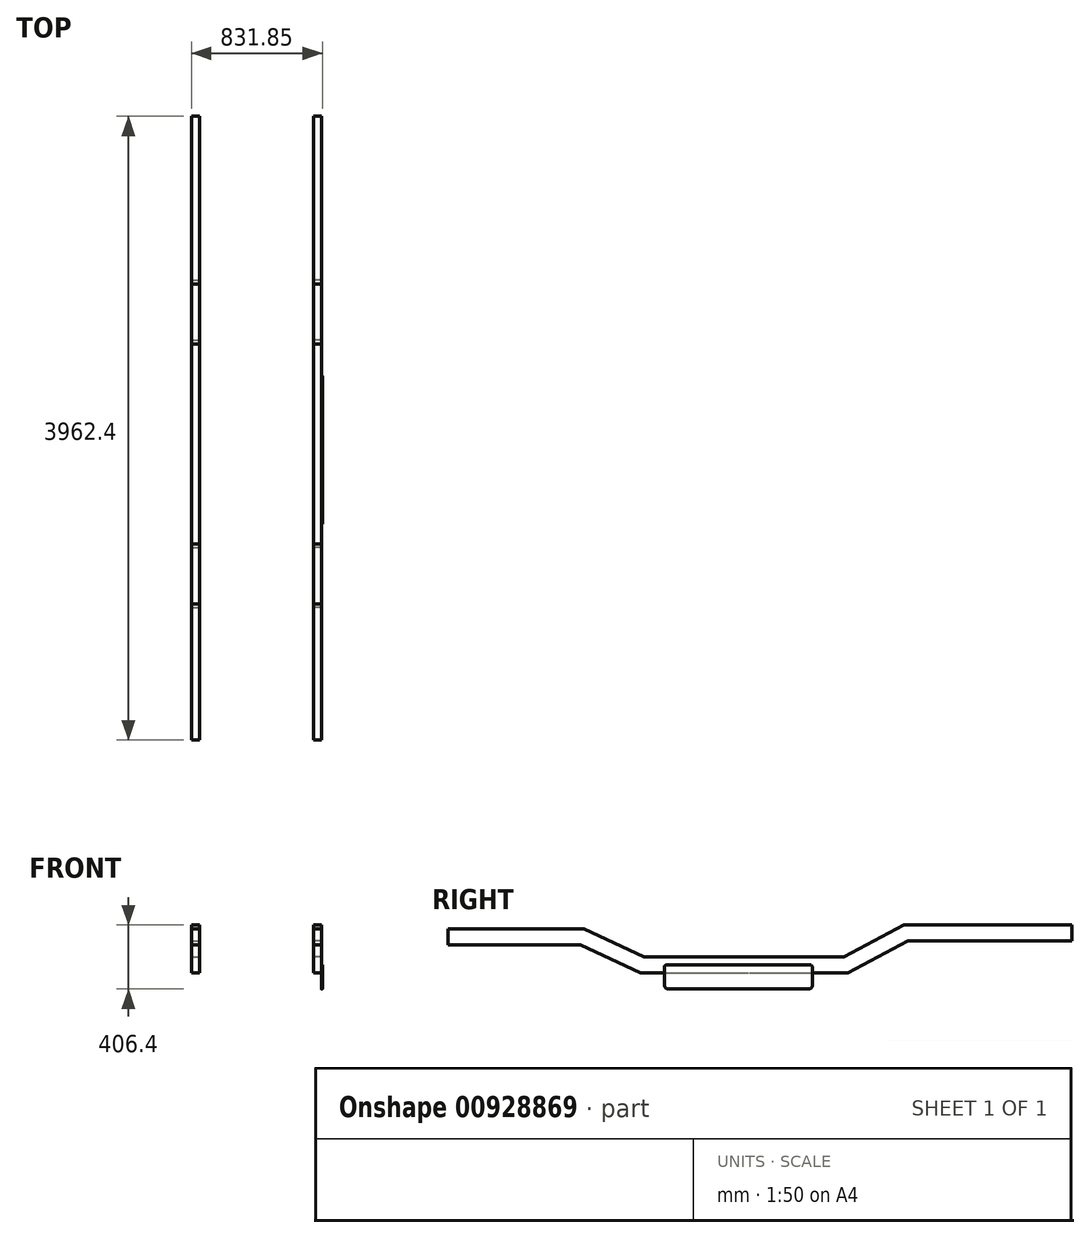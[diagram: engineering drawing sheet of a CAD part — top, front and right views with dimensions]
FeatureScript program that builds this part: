
annotation { "Feature Type Name" : "Feature", "Feature Type Description" : "" }
export const myFeature = defineFeature(function(context is Context, id is Id, definition is map)
    precondition{}
    {
        {
            var Q0;
            Q0=qCreatedBy(makeId("Right.planeOp"),FACE);
            var sketch = newSketch(context, id + "F0", { "sketchPlane" : qUnion([Q0])});
            skLineSegment(sketch, "E0", {"start": v(-1881.03, 279.4) * mm, "end": v(-1017.43, 279.4) * mm});
            skLineSegment(sketch, "E1", {"start": v(-1881.03, 177.8) * mm, "end": v(-1039.97, 177.8) * mm});
            skLineSegment(sketch, "E2", {"start": v(-1881.03, 177.8) * mm, "end": v(-1881.03, 279.4) * mm});
            skLineSegment(sketch, "E3", {"start": v(-1039.97, 177.8) * mm, "end": v(-658.97, 0) * mm});
            skLineSegment(sketch, "E4", {"start": v(-658.97, 0) * mm, "end": v(658.97, 0) * mm});
            skLineSegment(sketch, "E5", {"start": v(658.97, 0) * mm, "end": v(1039.97, 203.2) * mm});
            skLineSegment(sketch, "E6", {"start": v(1039.97, 203.2) * mm, "end": v(2081.37, 203.2) * mm});
            skLineSegment(sketch, "E7", {"start": v(2081.37, 203.2) * mm, "end": v(2081.37, 304.8) * mm});
            skLineSegment(sketch, "E8", {"start": v(2081.37, 304.8) * mm, "end": v(1014.57, 304.8) * mm});
            skLineSegment(sketch, "E9", {"start": v(1014.57, 304.8) * mm, "end": v(633.57, 101.6) * mm});
            skLineSegment(sketch, "E10", {"start": v(633.57, 101.6) * mm, "end": v(-636.43, 101.6) * mm});
            skLineSegment(sketch, "E11", {"start": v(-636.43, 101.6) * mm, "end": v(-1017.43, 279.4) * mm});
            skLineSegment(sketch, "E12", {"start": v(-849.47, 88.9) * mm, "end": v(-806.5, 180.97) * mm, "construction": true});
            skLineSegment(sketch, "E13", {"start": v(849.47, 101.6) * mm, "end": v(801.66, 191.25) * mm, "construction": true});
            skSolve(sketch);
        }
        {
            var Q0;
            Q0 = qSketchRegion(id + "F0", true);
            var Q1;
            Q1 = qSketchRegion(id + "F2", true);
            extrude(context, id + "F1", {"entities" : qUnion([Q0, Q1]), "oppositeDirection" : true, "depth" : 412.75 * mm, "offsetDistance" : 25.4 * mm});
        }
        {
            var Q0;
            Q0=makeQuery(id+"F1.opExtrude","SWEPT_FACE",FACE,{"disambiguationData":[OSD([sQuery(id+"F0.wireOp",EDGE,"E10")])]});
            var sketch = newSketch(context, id + "F2", { "sketchPlane" : qUnion([Q0])});
            skLineSegment(sketch, "E14", {"start": v(0, -2159) * mm, "end": v(0, 2159) * mm});
            skLineSegment(sketch, "E15", {"start": v(0, 2159) * mm, "end": v(-361.95, 2159) * mm});
            skLineSegment(sketch, "E16", {"start": v(-361.95, 2159) * mm, "end": v(-361.95, -2159) * mm});
            skLineSegment(sketch, "E17", {"start": v(-361.95, -2159) * mm, "end": v(0, -2159) * mm});
            skSolve(sketch);
        }
        {
            var Q0;
            Q0 = qSketchRegion(id + "F2", true);
            extrude(context, id + "F3", {"entities" : qUnion([Q0]), "operationType" : NewBodyOperationType.REMOVE, "endBound" : BoundingType.THROUGH_ALL, "oppositeDirection" : true, "depth" : 25.4 * mm, "offsetDistance" : 25.4 * mm});
        }
        {
            var Q0;
            Q0 = qSketchRegion(id + "F2", true);
            extrude(context, id + "F4", {"entities" : qUnion([Q0]), "operationType" : NewBodyOperationType.REMOVE, "endBound" : BoundingType.THROUGH_ALL, "depth" : 25.4 * mm, "offsetDistance" : 25.4 * mm});
        }
        {
            var Q0;
            Q0=makeQuery(id+"F1.opExtrude","SWEPT_BODY",BODY,{"disambiguationData":[OSD([sQuery(id+"F0.wireOp",EDGE,"E0"),sQuery(id+"F0.wireOp",EDGE,"E1"),sQuery(id+"F0.wireOp",EDGE,"E2"),sQuery(id+"F0.wireOp",EDGE,"E3"),sQuery(id+"F0.wireOp",EDGE,"E4"),sQuery(id+"F0.wireOp",EDGE,"E5"),sQuery(id+"F0.wireOp",EDGE,"E6"),sQuery(id+"F0.wireOp",EDGE,"E7"),sQuery(id+"F0.wireOp",EDGE,"E8"),sQuery(id+"F0.wireOp",EDGE,"E9"),sQuery(id+"F0.wireOp",EDGE,"E10"),sQuery(id+"F0.wireOp",EDGE,"E11")])]});
            var Q1;
            Q1=qCreatedBy(makeId("Right.planeOp"),FACE);
            mirror(context, id + "F5", {"entities" : qUnion([Q0]), "mirrorPlane" : qUnion([Q1])});
        }
        {
            var Q0;
            Q0=makeQuery(id+"F5.opPattern","COPY",FACE,{"derivedFrom":makeQuery(id+"F1.opExtrude","CAP_FACE",FACE,{"disambiguationData":[OSD([sQuery(id+"F0.wireOp",EDGE,"E0"),sQuery(id+"F0.wireOp",EDGE,"E1"),sQuery(id+"F0.wireOp",EDGE,"E2"),sQuery(id+"F0.wireOp",EDGE,"E3"),sQuery(id+"F0.wireOp",EDGE,"E4"),sQuery(id+"F0.wireOp",EDGE,"E5"),sQuery(id+"F0.wireOp",EDGE,"E6"),sQuery(id+"F0.wireOp",EDGE,"E7"),sQuery(id+"F0.wireOp",EDGE,"E8"),sQuery(id+"F0.wireOp",EDGE,"E9"),sQuery(id+"F0.wireOp",EDGE,"E10"),sQuery(id+"F0.wireOp",EDGE,"E11")])],"isStart":false}),"instanceName":"1"});
            var sketch = newSketch(context, id + "F6", { "sketchPlane" : qUnion([Q0])});
            skLineSegment(sketch, "E18.bottom", {"start": v(-495.3, 50.8) * mm, "end": v(419.1, 50.8) * mm});
            skLineSegment(sketch, "E18.top", {"start": v(-482.6, -101.6) * mm, "end": v(406.4, -101.6) * mm});
            skLineSegment(sketch, "E18.left", {"start": v(-508, 38.1) * mm, "end": v(-508, -76.2) * mm});
            skLineSegment(sketch, "E18.right", {"start": v(431.8, 38.1) * mm, "end": v(431.8, -76.2) * mm});
            skPoint(sketch, "E19.visualSharp", {"position": v(-508, -101.6) * mm});
            skArc(sketch, "E19.filletArc", {"start": v(-508, -76.2) * mm, "mid": v(-500.56, -94.16) * mm, "end": v(-482.6, -101.6) * mm});
            skPoint(sketch, "E20.visualSharp", {"position": v(431.8, -101.6) * mm});
            skArc(sketch, "E20.filletArc", {"start": v(406.4, -101.6) * mm, "mid": v(424.36, -94.16) * mm, "end": v(431.8, -76.2) * mm});
            skPoint(sketch, "E21.visualSharp", {"position": v(431.8, 50.8) * mm});
            skArc(sketch, "E21.filletArc", {"start": v(431.8, 38.1) * mm, "mid": v(428.08, 47.08) * mm, "end": v(419.1, 50.8) * mm});
            skPoint(sketch, "E22.visualSharp", {"position": v(-508, 50.8) * mm});
            skArc(sketch, "E22.filletArc", {"start": v(-495.3, 50.8) * mm, "mid": v(-504.28, 47.08) * mm, "end": v(-508, 38.1) * mm});
            skSolve(sketch);
        }
        {
            var Q0;
            Q0 = qSketchRegion(id + "F6", true);
            extrude(context, id + "F7", {"entities" : qUnion([Q0]), "depth" : 6.35 * mm, "offsetDistance" : 25.4 * mm});
        }
    });
